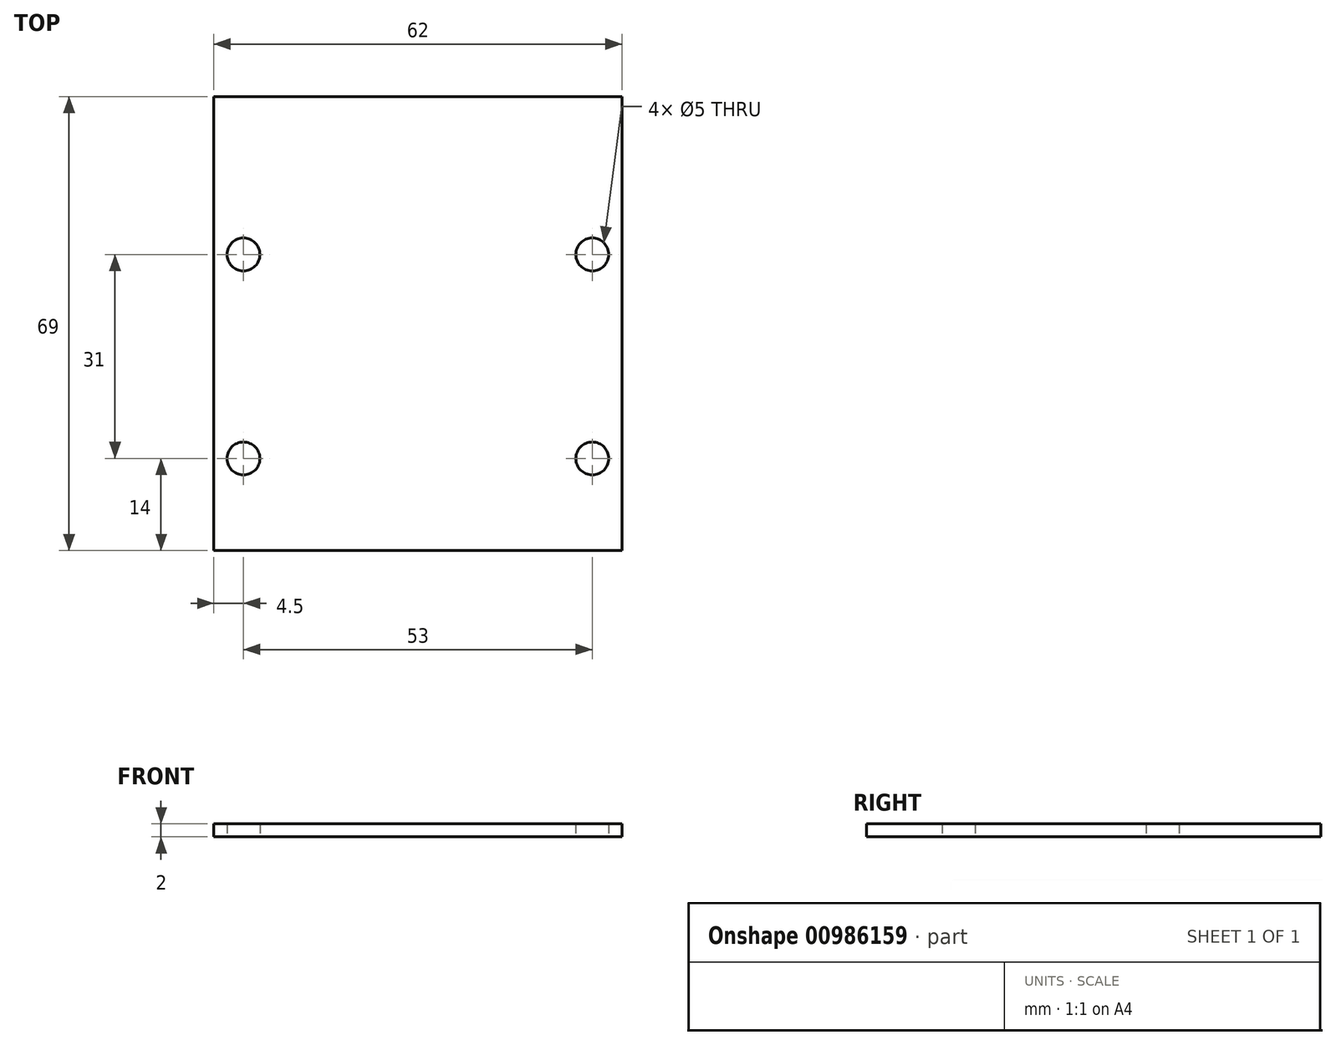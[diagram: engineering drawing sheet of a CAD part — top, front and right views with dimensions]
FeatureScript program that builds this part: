
annotation { "Feature Type Name" : "Feature", "Feature Type Description" : "" }
export const myFeature = defineFeature(function(context is Context, id is Id, definition is map)
    precondition{}
    {
        {
            var Q0;
            Q0=qCreatedBy(makeId("Top.planeOp"),FACE);
            var sketch = newSketch(context, id + "F0", { "sketchPlane" : qUnion([Q0])});
            skLineSegment(sketch, "E0.bottom", {"start": v(0, 0) * mm, "end": v(62, 0) * mm});
            skLineSegment(sketch, "E0.top", {"start": v(0, 69) * mm, "end": v(62, 69) * mm});
            skLineSegment(sketch, "E0.left", {"start": v(0, 0) * mm, "end": v(0, 69) * mm});
            skLineSegment(sketch, "E0.right", {"start": v(62, 0) * mm, "end": v(62, 69) * mm});
            skCircle(sketch, "E1", {"center": v(4.5, 14) * mm, "radius": 2.5 * mm});
            skCircle(sketch, "E2", {"center": v(4.5, 45) * mm, "radius": 2.5 * mm});
            skCircle(sketch, "E3", {"center": v(57.5, 45) * mm, "radius": 2.5 * mm});
            skCircle(sketch, "E4", {"center": v(57.5, 14) * mm, "radius": 2.5 * mm});
            skSolve(sketch);
        }
        {
            var Q0;
            Q0=makeQuery(id+"F0.imprint","IMPRINT",FACE,{"disambiguationData":[TD([[makeQuery(id+"F0.imprint","IMPRINT",EDGE,{"derivedFrom":sQuery(id+"F0.wireOp",EDGE,"E0.bottom")}),1.0]])]});
            extrude(context, id + "F1", {"entities" : qUnion([Q0]), "depth" : 2 * mm, "offsetDistance" : 25 * mm});
        }
    });
